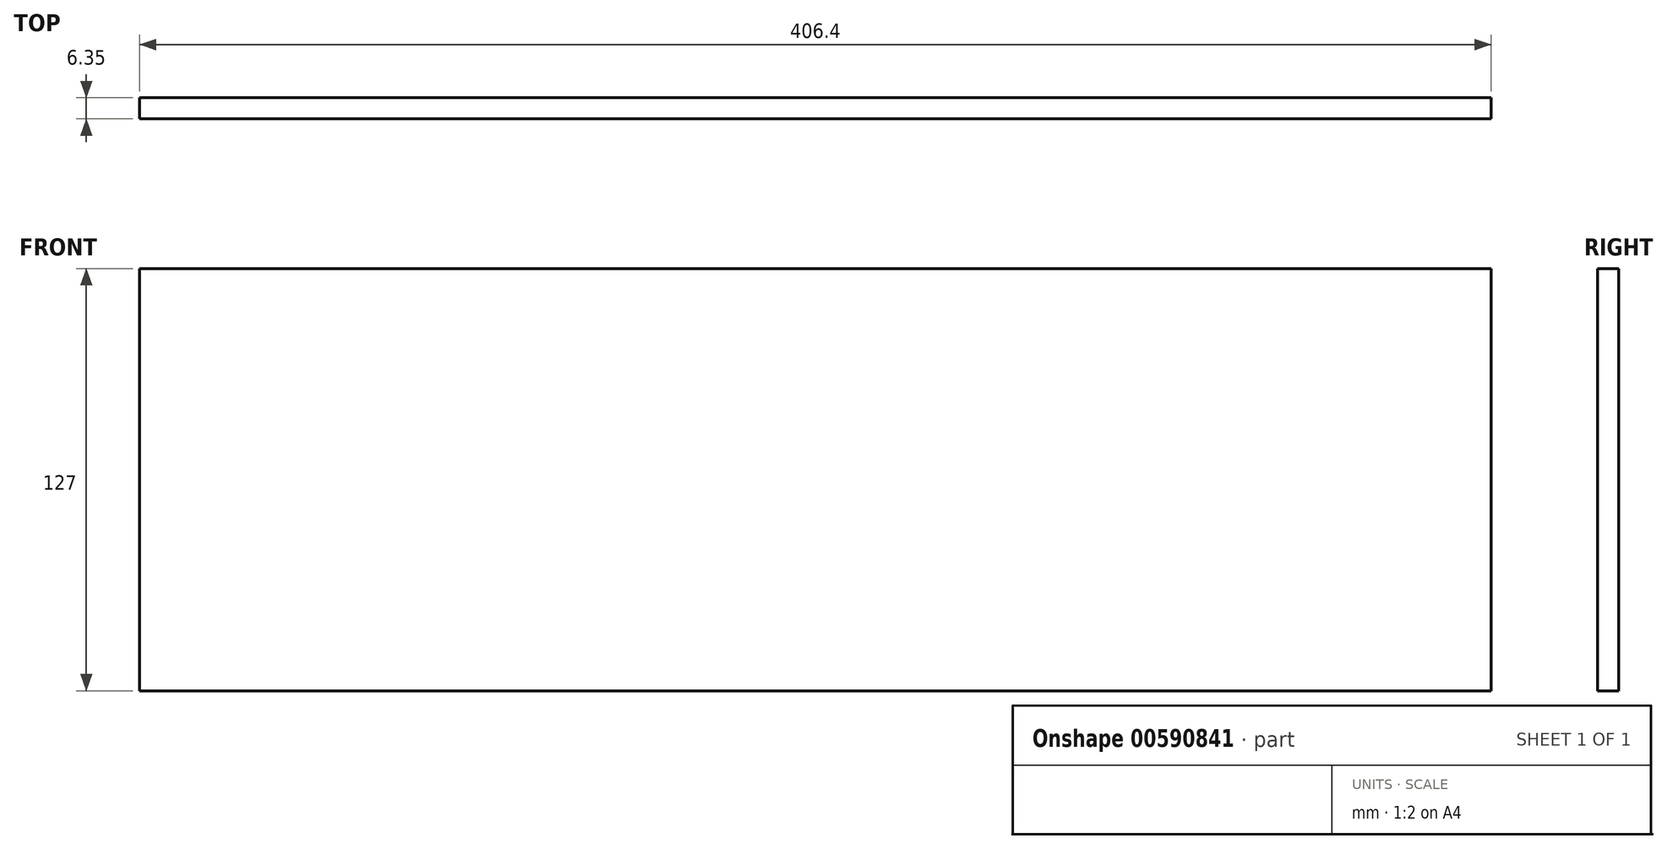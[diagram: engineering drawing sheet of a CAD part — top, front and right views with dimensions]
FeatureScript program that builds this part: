
annotation { "Feature Type Name" : "Feature", "Feature Type Description" : "" }
export const myFeature = defineFeature(function(context is Context, id is Id, definition is map)
    precondition{}
    {
        {
            var Q0;
            Q0=qCreatedBy(makeId("Front.planeOp"),FACE);
            var sketch = newSketch(context, id + "F0", { "sketchPlane" : qUnion([Q0])});
            skLineSegment(sketch, "E0.bottom", {"start": v(185.21, -188.5) * mm, "end": v(-221.19, -188.5) * mm});
            skLineSegment(sketch, "E0.top", {"start": v(185.21, -315.5) * mm, "end": v(-221.19, -315.5) * mm});
            skLineSegment(sketch, "E0.left", {"start": v(185.21, -188.5) * mm, "end": v(185.21, -315.5) * mm});
            skLineSegment(sketch, "E0.right", {"start": v(-221.19, -188.5) * mm, "end": v(-221.19, -315.5) * mm});
            skSolve(sketch);
        }
        {
            var Q0;
            Q0=makeQuery(id+"F0.imprint","IMPRINT",FACE,{"disambiguationData":[TD([[makeQuery(id+"F0.imprint","IMPRINT",EDGE,{"derivedFrom":sQuery(id+"F0.wireOp",EDGE,"E0.bottom")}),1.0]])]});
            extrude(context, id + "F1", {"entities" : qUnion([Q0]), "depth" : 6.35 * mm, "offsetDistance" : 25.4 * mm});
        }
    });
